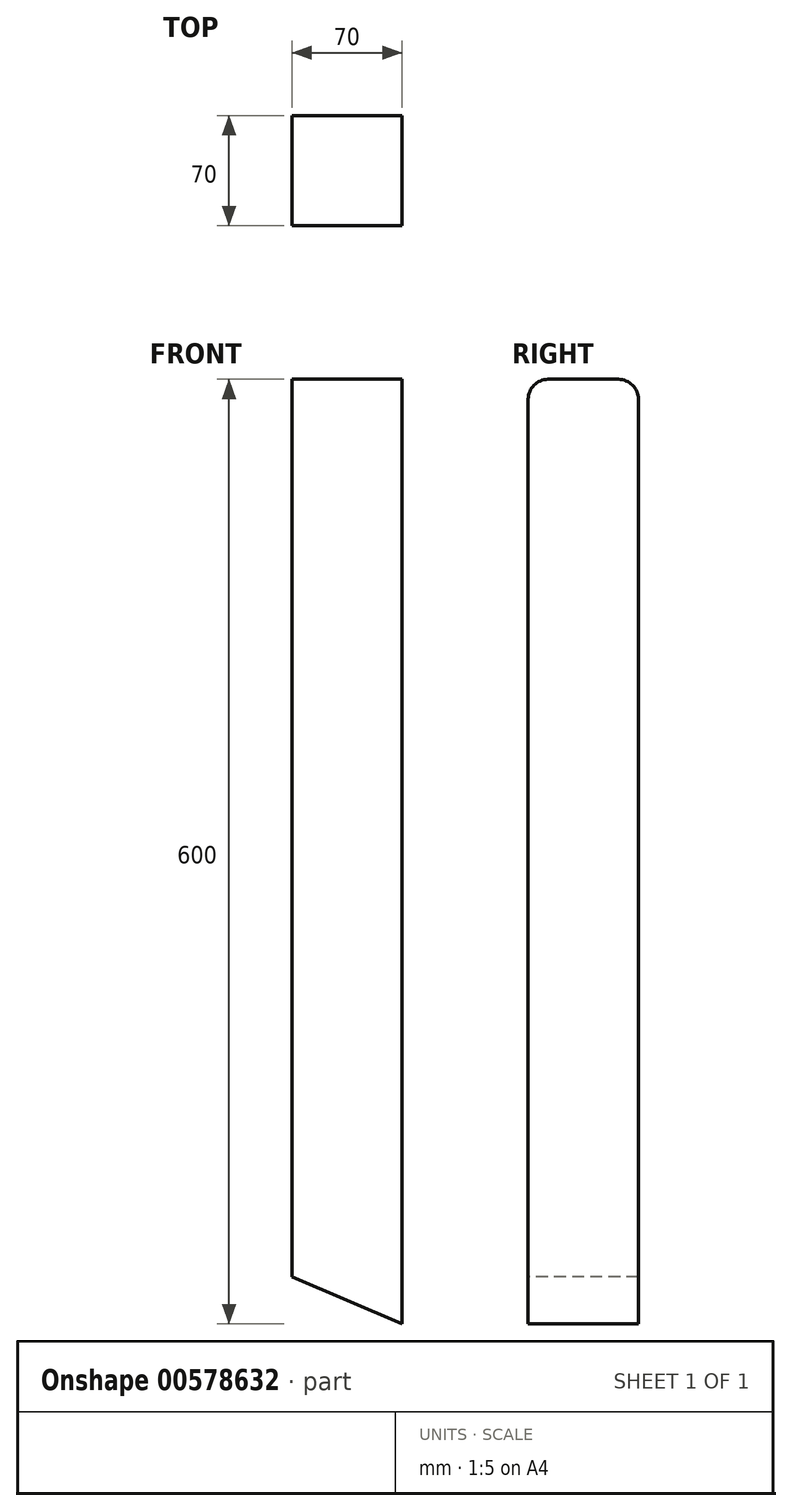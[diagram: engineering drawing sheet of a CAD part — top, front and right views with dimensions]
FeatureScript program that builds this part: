
annotation { "Feature Type Name" : "Feature", "Feature Type Description" : "" }
export const myFeature = defineFeature(function(context is Context, id is Id, definition is map)
    precondition{}
    {
        {
            var Q0;
            Q0=qCreatedBy(makeId("Front.planeOp"),FACE);
            var sketch = newSketch(context, id + "F0", { "sketchPlane" : qUnion([Q0])});
            skLineSegment(sketch, "E0.bottom", {"start": v(-35, 300) * mm, "end": v(35, 300) * mm});
            skLineSegment(sketch, "E0.top", {"start": v(-35, -300) * mm, "end": v(35, -300) * mm});
            skLineSegment(sketch, "E0.left", {"start": v(-35, 300) * mm, "end": v(-35, -300) * mm});
            skLineSegment(sketch, "E0.right", {"start": v(35, 300) * mm, "end": v(35, -300) * mm});
            skPoint(sketch, "E0.middle", {"position": v(0, 0) * mm});
            skSolve(sketch);
        }
        {
            var Q0;
            Q0=makeQuery(id+"F0.imprint","IMPRINT",FACE,{"disambiguationData":[TD([[makeQuery(id+"F0.imprint","IMPRINT",EDGE,{"derivedFrom":sQuery(id+"F0.wireOp",EDGE,"E0.bottom")}),-1.0]])]});
            extrude(context, id + "F1", {"entities" : qUnion([Q0]), "endBound" : BoundingType.SYMMETRIC, "depth" : 70 * mm, "offsetDistance" : 25.4 * mm});
        }
        {
            var Q0;
            Q0=makeQuery(id+"F1.opExtrude","CAP_EDGE",EDGE,{"disambiguationData":[OSD([sQuery(id+"F0.wireOp",EDGE,"E0.bottom")])],"isStart":false});
            var Q1;
            Q1=makeQuery(id+"F1.opExtrude","CAP_EDGE",EDGE,{"disambiguationData":[OSD([sQuery(id+"F0.wireOp",EDGE,"E0.bottom")])],"isStart":true});
            fillet(context, id + "F2", {"entities" : qUnion([Q0, Q1]), "radius" : 12.7 * mm, "tangentPropagation" : true, "allowEdgeOverflow" : false});
        }
        {
            var Q0;
            Q0=makeQuery(id+"F1.opExtrude","CAP_FACE",FACE,{"disambiguationData":[OSD([sQuery(id+"F0.wireOp",EDGE,"E0.bottom"),sQuery(id+"F0.wireOp",EDGE,"E0.top"),sQuery(id+"F0.wireOp",EDGE,"E0.left"),sQuery(id+"F0.wireOp",EDGE,"E0.right")])],"isStart":false});
            var sketch = newSketch(context, id + "F3", { "sketchPlane" : qUnion([Q0])});
            skLineSegment(sketch, "E1", {"start": v(-35, -270) * mm, "end": v(-35, -300) * mm});
            skLineSegment(sketch, "E2", {"start": v(-35, -270) * mm, "end": v(35, -300) * mm});
            skLineSegment(sketch, "E3", {"start": v(-35, -300) * mm, "end": v(35, -300) * mm});
            skSolve(sketch);
        }
        {
            var Q0;
            Q0=makeQuery(id+"F3.imprint","IMPRINT",FACE,{"disambiguationData":[TD([[makeQuery(id+"F3.imprint","IMPRINT",EDGE,{"derivedFrom":sQuery(id+"F3.wireOp",EDGE,"E1")}),1.0]])]});
            extrude(context, id + "F4", {"entities" : qUnion([Q0]), "operationType" : NewBodyOperationType.REMOVE, "endBound" : BoundingType.SYMMETRIC, "oppositeDirection" : true, "depth" : 144.78 * mm, "offsetDistance" : 25.4 * mm});
        }
    });
